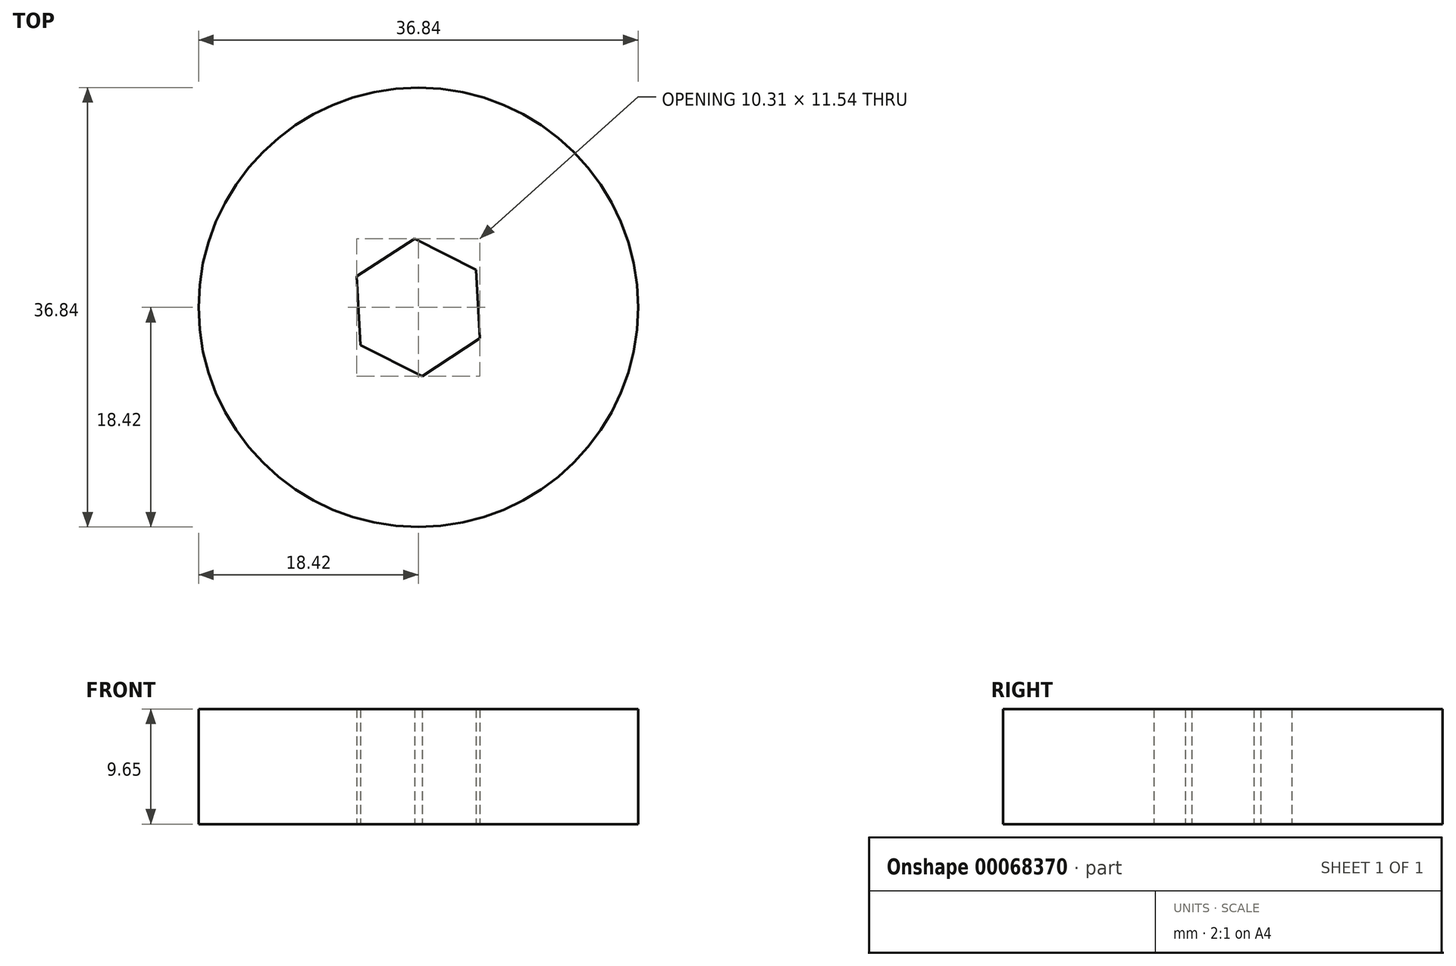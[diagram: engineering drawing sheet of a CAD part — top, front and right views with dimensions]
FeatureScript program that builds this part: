
annotation { "Feature Type Name" : "Feature", "Feature Type Description" : "" }
export const myFeature = defineFeature(function(context is Context, id is Id, definition is map)
    precondition{}
    {
        {
            var Q0;
            Q0=qCreatedBy(makeId("Top.planeOp"),FACE);
            var sketch = newSketch(context, id + "F0", { "sketchPlane" : qUnion([Q0])});
            skCircle(sketch, "E0", {"center": v(0, 0) * mm, "radius": 18.41 * mm});
            skCircle(sketch, "E1.cCircle", {"center": v(0, 0) * mm, "radius": 5 * mm, "construction": true});
            skLineSegment(sketch, "E1.0", {"start": v(5.16, -2.6) * mm, "end": v(0.32, -5.77) * mm});
            skLineSegment(sketch, "E1.1", {"start": v(0.32, -5.77) * mm, "end": v(-4.84, -3.16) * mm});
            skLineSegment(sketch, "E1.2", {"start": v(-4.84, -3.16) * mm, "end": v(-5.16, 2.6) * mm});
            skLineSegment(sketch, "E1.3", {"start": v(-5.16, 2.6) * mm, "end": v(-0.32, 5.77) * mm});
            skLineSegment(sketch, "E1.4", {"start": v(-0.32, 5.77) * mm, "end": v(4.84, 3.16) * mm});
            skLineSegment(sketch, "E1.5", {"start": v(4.84, 3.16) * mm, "end": v(5.16, -2.6) * mm});
            skPoint(sketch, "E1.0.midPoint", {"position": v(2.74, -4.19) * mm});
            skLineSegment(sketch, "E2", {"start": v(-5.16, 2.6) * mm, "end": v(0.32, -5.77) * mm, "construction": true});
            skSolve(sketch);
        }
        {
            var Q0;
            Q0=makeQuery(id+"F0.imprint","IMPRINT",FACE,{"disambiguationData":[TD([[makeQuery(id+"F0.imprint","IMPRINT",EDGE,{"derivedFrom":sQuery(id+"F0.wireOp",EDGE,"E0")}),1.0]])]});
            extrude(context, id + "F1", {"entities" : qUnion([Q0]), "depth" : 9.65 * mm});
        }
    });
